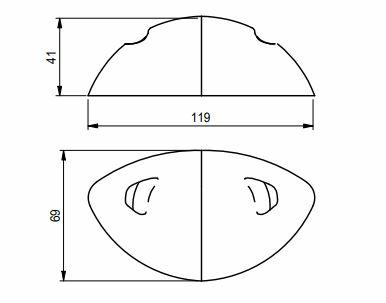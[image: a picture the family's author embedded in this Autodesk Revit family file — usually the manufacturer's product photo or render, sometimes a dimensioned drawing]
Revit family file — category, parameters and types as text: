
# Revit family: R-MBD-492
name_source: partatom
category: Portes
units: mm (PartAtom-declared; Revit-internal decimal feet)

## family parameters
Couper avec des vides une fois chargée = Non
Hôte = Mur
Partagée = Non
Repère de localisation dans la pièce = Oui
Toujours verticalement = Oui

## types (1)
- MBD-492
    1 Vantail = Oui
    2 Vantaux = Non
    A.E.V = non
    Acoustique = non
    Anti-Effraction = non
    Certification = D.A.S. Mode 2 certifié NF
    Code_MAJ = 2303130305MBD492
    Coloris_Chants = BER
    Coloris_Dormant = Hêtre
    Coloris_Face_Cote_Oppose_Ouverture = Prépeint
    Coloris_Face_Cote_Ouverture = Prépeint
    Construction analytique = <Aucun>
    DAS = Oui
    DC Larg Feuillure = 12 mm  [stored 0.0393701 ft]
    DC Pivot Vantail = 60 mm  [stored 0.19685 ft]
    Description = Bloc-porte bois D.A.S. 1 vantail SP51 avec pivot linteau motorisé encastré, double action / va-et-vient, EI60, D.A.S. certifié NF, sur huisserie bois sans montant avec fileur
    Définir les propriétés thermiques par = Type schématique
    Ep Profil Pose Tunnel = 118 mm
    Ep Strat Vantail = 1 mm  [stored 0.00328084 ft]
    Ep Vantail = 46 mm  [stored 0.150919 ft]
    Epaisseur_Rainure à brique = 8 mm  [stored 0.0262467 ft]
    Fabricant = MALERBA
    Fiche_Produit = MBD-492
    Fileur = Oui
    Hauteur_Tableau = 2125 mm
    Hauteur_Vantaux_Souhaitée = 2040 mm  [stored 6.69291 ft]
    Jeu_1 = 0 mm  [stored 0 ft]
    Jeu_2 = 0 mm  [stored 0 ft]
    Jeu_Côté_Articulation_Vantail = 8 mm  [stored 0.0262467 ft]
    Jeu_Côté_Fermeture_Vantail = 8 mm  [stored 0.0262467 ft]
    Jeu_Haut = 3 mm  [stored 0.00984252 ft]
    Larg Profil = 58 mm  [stored 0.190289 ft]
    Larg Profil Avec Fileur = 20 mm  [stored 0.0656168 ft]
    Larg Profil Trav = 76 mm  [stored 0.249344 ft]
    Largeur = 0 mm  [stored 0 ft]
    Largeur_Vantail_Semi_Fixe_Souhaitée = 930 mm  [stored 3.05118 ft]
    Largeur_Vantail_Service_Souhaitée = 930 mm  [stored 3.05118 ft]
    Mat APD = Caoutchouc noir
    Mat Parclose = BER 2
    Mat Parclose Métal = Peinture Laquée PMT - Blanc Pur - RAL 9010
    Materiaux_Dominant = Bois
    Modèle = Va et vient
    Montant_VV = Non
    Note d'identification = 1V EI60/SP51 DAS - LINTEAU MOTORISE - SANS MONTANT AVEC FILEUR
    Pivot linteau motorisé = Oui
    Profondeur_Rainure à brique = 5 mm  [stored 0.0164042 ft]
    Reference_Commerciale = 1V SP51/DA LINTEAU OP
    Resistance_Feu = EI30
    Sans_Montants = Non
    Sens_Feu = Recto / Verso
    Thermique (W/m2.°K) = 0
    URL = https://www.malerba.fr
    X_Axe Pivot = 88 mm  [stored 0.288714 ft]
    X_DC seuil = 9 mm  [stored 0.0295276 ft]
    X_Inv_DC Larg Feuillure_1V Montant = 0 mm  [stored 0 ft]

note: [stored X ft] marks values corroborated as IEEE doubles in the binary element streams (Revit-internal decimal feet)

## geometry (parser evidence)
native form markers: Blend x14
no freeform markers — native parametric forms only
